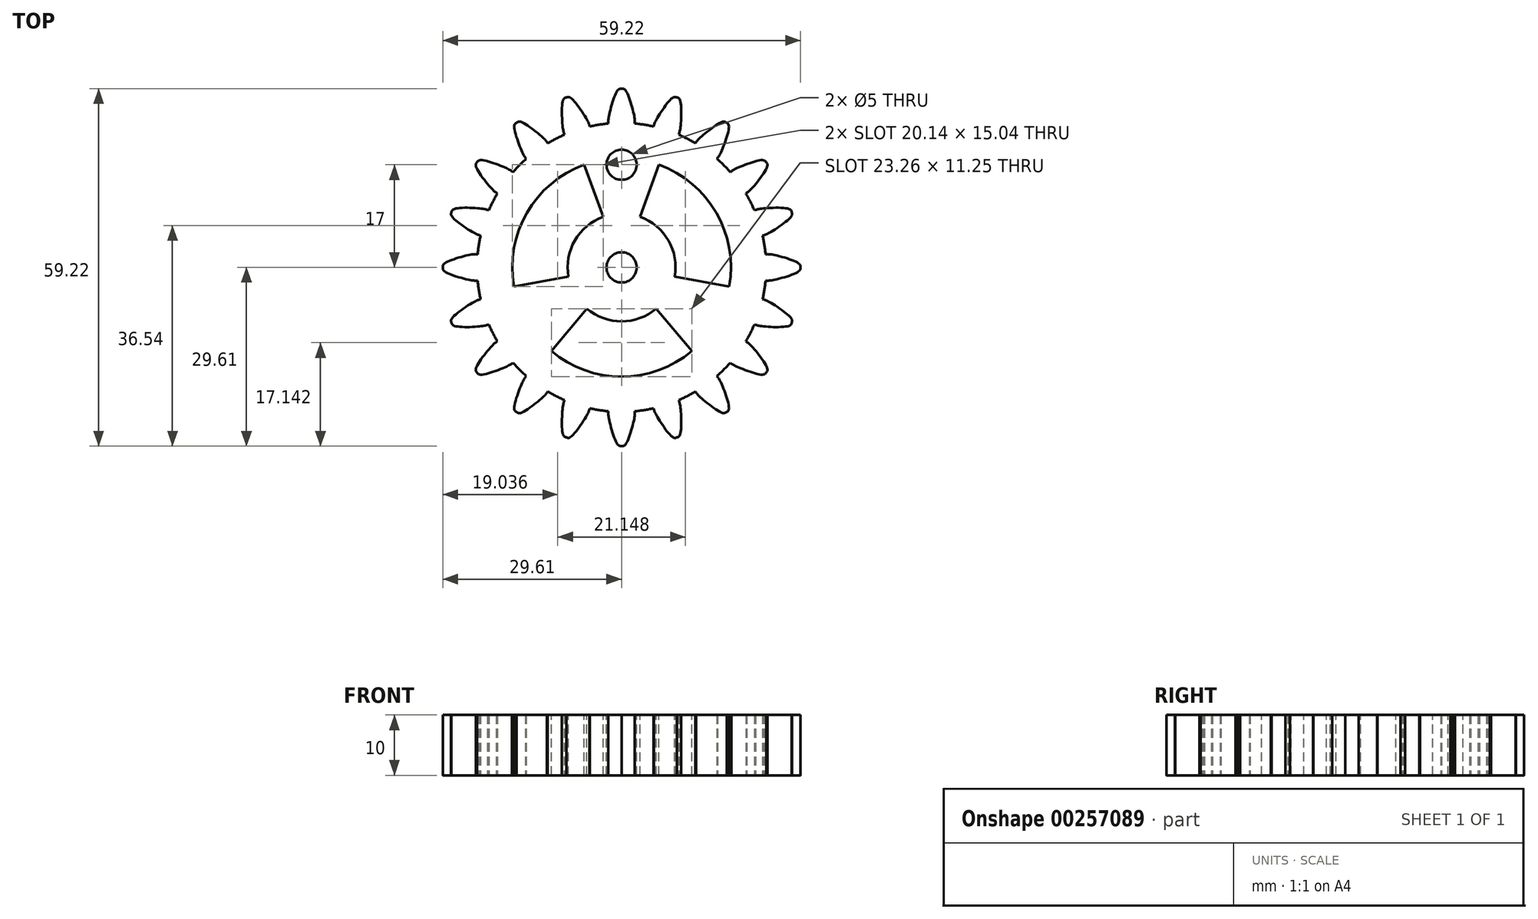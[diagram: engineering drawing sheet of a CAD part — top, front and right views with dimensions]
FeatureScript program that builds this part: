
annotation { "Feature Type Name" : "Feature", "Feature Type Description" : "" }
export const myFeature = defineFeature(function(context is Context, id is Id, definition is map)
    precondition{}
    {
        {
            var Q0;
            Q0=qCreatedBy(makeId("Top.planeOp"),FACE);
            var sketch = newSketch(context, id + "F0", { "sketchPlane" : qUnion([Q0])});
            skLineSegment(sketch, "E0.bottom", {"start": v(-22.39, -2.2) * mm, "end": v(-24.04, -2.2) * mm});
            skLineSegment(sketch, "E0.top", {"start": v(-22.39, 2.2) * mm, "end": v(-24.04, 2.2) * mm});
            skLineSegment(sketch, "E0.left", {"start": v(-22.39, -2.2) * mm, "end": v(-22.39, 2.2) * mm});
            skLineSegment(sketch, "E0.right", {"start": v(-24.04, -2.2) * mm, "end": v(-24.04, 2.2) * mm});
            skPoint(sketch, "E0.middle", {"position": v(-23.21, 0) * mm});
            skFitSpline(sketch, "E1", {"points": [v(-24.04, 2.2) * mm, v(-25.02, 2.1) * mm, v(-29.35, 0.63) * mm, v(-29.6, 0) * mm], "startDerivative": vector(-2.71, 0.04) * mm, "endDerivative": vector(0.07, -2.94) * mm});
            skLineSegment(sketch, "E2", {"start": v(-29.6, 0) * mm, "end": v(-24.04, 0) * mm});
            skFitSpline(sketch, "E3.MirrorCS", {"points": [v(-24.04, -2.2) * mm, v(-25.02, -2.1) * mm, v(-29.35, -0.63) * mm, v(-29.6, 0) * mm], "startDerivative": vector(-2.71, -0.04) * mm, "endDerivative": vector(0.07, 2.94) * mm});
            skCircle(sketch, "E4", {"center": v(0, 0) * mm, "radius": 5.34 * mm});
            skSolve(sketch);
        }
        {
            var Q0;
            Q0=makeQuery(id+"F0.imprint","IMPRINT",FACE,{"disambiguationData":[TD([[makeQuery(id+"F0.imprint","IMPRINT",EDGE,{"derivedFrom":sQuery(id+"F0.wireOp",EDGE,"E4")}),1.0]])]});
            extrude(context, id + "F1", {"entities" : qUnion([Q0]), "depth" : 10 * mm});
        }
        {
            var Q0;
            {var subQ0=sQuery(id+"F0.wireOp",EDGE,"E1");Q0=makeQuery(id+"F0.imprint","IMPRINT",FACE,{"disambiguationData":[TD([[makeQuery(id+"F0.imprint","IMPRINT",EDGE,{"derivedFrom":subQ0}),1.0]])]});}
            var Q1;
            {var subQ1=sQuery(id+"F0.wireOp",EDGE,"E0.bottom");Q1=makeQuery(id+"F0.imprint","IMPRINT",FACE,{"disambiguationData":[TD([[makeQuery(id+"F0.imprint","IMPRINT",EDGE,{"derivedFrom":subQ1}),-1.0]])]});}
            var Q2;
            {var subQ2=sQuery(id+"F0.wireOp",EDGE,"E2");Q2=makeQuery(id+"F0.imprint","IMPRINT",FACE,{"disambiguationData":[TD([[makeQuery(id+"F0.imprint","IMPRINT",EDGE,{"derivedFrom":subQ2}),-1.0]])]});}
            extrude(context, id + "F2", {"entities" : qUnion([Q0, Q1, Q2]), "depth" : 10 * mm});
        }
        {
            var Q0;
            Q0=makeQuery(id+"F2.opExtrude","SWEPT_BODY",BODY,{"disambiguationData":[OSD([sQuery(id+"F0.wireOp",EDGE,"E0.bottom"),sQuery(id+"F0.wireOp",EDGE,"E0.top"),sQuery(id+"F0.wireOp",EDGE,"E0.left"),sQuery(id+"F0.wireOp",EDGE,"E1"),sQuery(id+"F0.wireOp",EDGE,"E3.MirrorCS")])]});
            var Q1;
            Q1=makeQuery(id+"F1.opExtrude","CAP_EDGE",EDGE,{"disambiguationData":[OSD([sQuery(id+"F0.wireOp",EDGE,"E4")])],"isStart":false});
            circularPattern(context, id + "F3", {"entities" : qUnion([Q0]), "axis" : qUnion([Q1]), "angle" : 360 * degree, "instanceCount" : 20, "equalSpace" : true});
        }
        {
            var Q0;
            Q0=qCreatedBy(makeId("Top.planeOp"),FACE);
            var sketch = newSketch(context, id + "F4", { "sketchPlane" : qUnion([Q0])});
            skCircle(sketch, "E5", {"center": v(0, 0) * mm, "radius": 23.92 * mm});
            skSolve(sketch);
        }
        {
            var Q0;
            Q0=makeQuery(id+"F4.imprint","IMPRINT",FACE,{"disambiguationData":[TD([[makeQuery(id+"F4.imprint","IMPRINT",EDGE,{"derivedFrom":sQuery(id+"F4.wireOp",EDGE,"E5")}),1.0]])]});
            extrude(context, id + "F5", {"entities" : qUnion([Q0]), "operationType" : NewBodyOperationType.ADD, "depth" : 10 * mm});
        }
        {
            var Q0;
            {var subQ0=makeQuery(id+"F2.opExtrude","CAP_FACE",FACE,{"disambiguationData":[OSD([sQuery(id+"F0.wireOp",EDGE,"E0.bottom"),sQuery(id+"F0.wireOp",EDGE,"E0.top"),sQuery(id+"F0.wireOp",EDGE,"E0.left"),sQuery(id+"F0.wireOp",EDGE,"E1"),sQuery(id+"F0.wireOp",EDGE,"E3.MirrorCS")])],"isStart":false});Q0=makeQuery(id+"F5.boolean.opBoolean","MERGE",FACE,{"derivedFrom":[makeQuery(id+"F1.opExtrude","CAP_FACE",FACE,{"disambiguationData":[OSD([sQuery(id+"F0.wireOp",EDGE,"E4")])],"isStart":false}),subQ0,makeQuery(id+"F3.opPattern","COPY",FACE,{"derivedFrom":subQ0,"instanceName":"1"}),makeQuery(id+"F3.opPattern","COPY",FACE,{"derivedFrom":subQ0,"instanceName":"2"}),makeQuery(id+"F3.opPattern","COPY",FACE,{"derivedFrom":subQ0,"instanceName":"3"}),makeQuery(id+"F3.opPattern","COPY",FACE,{"derivedFrom":subQ0,"instanceName":"4"}),makeQuery(id+"F3.opPattern","COPY",FACE,{"derivedFrom":subQ0,"instanceName":"5"}),makeQuery(id+"F3.opPattern","COPY",FACE,{"derivedFrom":subQ0,"instanceName":"6"}),makeQuery(id+"F3.opPattern","COPY",FACE,{"derivedFrom":subQ0,"instanceName":"7"}),makeQuery(id+"F3.opPattern","COPY",FACE,{"derivedFrom":subQ0,"instanceName":"8"}),makeQuery(id+"F3.opPattern","COPY",FACE,{"derivedFrom":subQ0,"instanceName":"9"}),makeQuery(id+"F3.opPattern","COPY",FACE,{"derivedFrom":subQ0,"instanceName":"10"}),makeQuery(id+"F3.opPattern","COPY",FACE,{"derivedFrom":subQ0,"instanceName":"11"}),makeQuery(id+"F3.opPattern","COPY",FACE,{"derivedFrom":subQ0,"instanceName":"12"}),makeQuery(id+"F3.opPattern","COPY",FACE,{"derivedFrom":subQ0,"instanceName":"13"}),makeQuery(id+"F3.opPattern","COPY",FACE,{"derivedFrom":subQ0,"instanceName":"14"}),makeQuery(id+"F3.opPattern","COPY",FACE,{"derivedFrom":subQ0,"instanceName":"15"}),makeQuery(id+"F5.opExtrude","CAP_FACE",FACE,{"disambiguationData":[OSD([sQuery(id+"F4.wireOp",EDGE,"E5")])],"isStart":false})]});}
            var sketch = newSketch(context, id + "F6", { "sketchPlane" : qUnion([Q0])});
            skLineSegment(sketch, "E6", {"start": v(0, 0) * mm, "end": v(0, -22.46) * mm, "construction": true});
            skArc(sketch, "E7", {"start": v(-11.63, -13.86) * mm, "mid": v(0, -18.1) * mm, "end": v(11.63, -13.86) * mm});
            skArc(sketch, "E8", {"start": v(-5.74, -6.84) * mm, "mid": v(0, -8.93) * mm, "end": v(5.74, -6.84) * mm});
            skLineSegment(sketch, "E9", {"start": v(-5.74, -6.84) * mm, "end": v(-11.63, -13.86) * mm});
            skLineSegment(sketch, "E10", {"start": v(5.74, -6.84) * mm, "end": v(11.63, -13.86) * mm});
            skArc(sketch, "E11.1.0", {"start": v(8.8, -1.55) * mm, "mid": v(7.74, 4.47) * mm, "end": v(3.06, 8.4) * mm});
            skLineSegment(sketch, "E11.1.1", {"start": v(8.8, -1.55) * mm, "end": v(17.82, -3.14) * mm});
            skArc(sketch, "E11.1.2", {"start": v(17.82, -3.14) * mm, "mid": v(15.67, 9.05) * mm, "end": v(6.19, 17) * mm});
            skLineSegment(sketch, "E11.1.3", {"start": v(3.06, 8.4) * mm, "end": v(6.19, 17) * mm});
            skArc(sketch, "E11.2.0", {"start": v(-3.06, 8.4) * mm, "mid": v(-7.74, 4.47) * mm, "end": v(-8.8, -1.55) * mm});
            skLineSegment(sketch, "E11.2.1", {"start": v(-3.06, 8.4) * mm, "end": v(-6.19, 17) * mm});
            skArc(sketch, "E11.2.2", {"start": v(-6.19, 17) * mm, "mid": v(-15.67, 9.05) * mm, "end": v(-17.82, -3.14) * mm});
            skLineSegment(sketch, "E11.2.3", {"start": v(-8.8, -1.55) * mm, "end": v(-17.82, -3.14) * mm});
            skSolve(sketch);
        }
        {
            var Q0;
            {var subQ0=makeQuery(id+"F2.opExtrude","CAP_FACE",FACE,{"disambiguationData":[OSD([sQuery(id+"F0.wireOp",EDGE,"E0.bottom"),sQuery(id+"F0.wireOp",EDGE,"E0.top"),sQuery(id+"F0.wireOp",EDGE,"E0.left"),sQuery(id+"F0.wireOp",EDGE,"E1"),sQuery(id+"F0.wireOp",EDGE,"E3.MirrorCS")])],"isStart":false});Q0=makeQuery(id+"F5.boolean.opBoolean","MERGE",FACE,{"derivedFrom":[makeQuery(id+"F1.opExtrude","CAP_FACE",FACE,{"disambiguationData":[OSD([sQuery(id+"F0.wireOp",EDGE,"E4")])],"isStart":false}),subQ0,makeQuery(id+"F3.opPattern","COPY",FACE,{"derivedFrom":subQ0,"instanceName":"1"}),makeQuery(id+"F3.opPattern","COPY",FACE,{"derivedFrom":subQ0,"instanceName":"2"}),makeQuery(id+"F3.opPattern","COPY",FACE,{"derivedFrom":subQ0,"instanceName":"3"}),makeQuery(id+"F3.opPattern","COPY",FACE,{"derivedFrom":subQ0,"instanceName":"4"}),makeQuery(id+"F3.opPattern","COPY",FACE,{"derivedFrom":subQ0,"instanceName":"5"}),makeQuery(id+"F3.opPattern","COPY",FACE,{"derivedFrom":subQ0,"instanceName":"6"}),makeQuery(id+"F3.opPattern","COPY",FACE,{"derivedFrom":subQ0,"instanceName":"7"}),makeQuery(id+"F3.opPattern","COPY",FACE,{"derivedFrom":subQ0,"instanceName":"8"}),makeQuery(id+"F3.opPattern","COPY",FACE,{"derivedFrom":subQ0,"instanceName":"9"}),makeQuery(id+"F3.opPattern","COPY",FACE,{"derivedFrom":subQ0,"instanceName":"10"}),makeQuery(id+"F3.opPattern","COPY",FACE,{"derivedFrom":subQ0,"instanceName":"11"}),makeQuery(id+"F3.opPattern","COPY",FACE,{"derivedFrom":subQ0,"instanceName":"12"}),makeQuery(id+"F3.opPattern","COPY",FACE,{"derivedFrom":subQ0,"instanceName":"13"}),makeQuery(id+"F3.opPattern","COPY",FACE,{"derivedFrom":subQ0,"instanceName":"14"}),makeQuery(id+"F3.opPattern","COPY",FACE,{"derivedFrom":subQ0,"instanceName":"15"}),makeQuery(id+"F5.opExtrude","CAP_FACE",FACE,{"disambiguationData":[OSD([sQuery(id+"F4.wireOp",EDGE,"E5")])],"isStart":false})]});}
            var sketch = newSketch(context, id + "F7", { "sketchPlane" : qUnion([Q0])});
            skCircle(sketch, "E12", {"center": v(0, 0) * mm, "radius": 2.5 * mm});
            skCircle(sketch, "E13.1.0.0", {"center": v(0, 17) * mm, "radius": 2.5 * mm});
            skLineSegment(sketch, "E13.direction1", {"start": v(0, 0) * mm, "end": v(0, 17) * mm, "construction": true});
            skSolve(sketch);
        }
        {
            var Q0;
            Q0=makeQuery(id+"F6.imprint","IMPRINT",FACE,{"disambiguationData":[TD([[makeQuery(id+"F6.imprint","IMPRINT",EDGE,{"derivedFrom":sQuery(id+"F6.wireOp",EDGE,"E11.2.0")}),-1.0]])]});
            var Q1;
            Q1=makeQuery(id+"F6.imprint","IMPRINT",FACE,{"disambiguationData":[TD([[makeQuery(id+"F6.imprint","IMPRINT",EDGE,{"derivedFrom":sQuery(id+"F6.wireOp",EDGE,"E7")}),1.0]])]});
            var Q2;
            Q2=makeQuery(id+"F6.imprint","IMPRINT",FACE,{"disambiguationData":[TD([[makeQuery(id+"F6.imprint","IMPRINT",EDGE,{"derivedFrom":sQuery(id+"F6.wireOp",EDGE,"E11.1.0")}),-1.0]])]});
            extrude(context, id + "F8", {"entities" : qUnion([Q0, Q1, Q2]), "operationType" : NewBodyOperationType.REMOVE, "endBound" : BoundingType.UP_TO_NEXT, "oppositeDirection" : true, "depth" : 25 * mm});
        }
        {
            var Q0;
            Q0=makeQuery(id+"F7.imprint","IMPRINT",FACE,{"disambiguationData":[TD([[makeQuery(id+"F7.imprint","IMPRINT",EDGE,{"derivedFrom":sQuery(id+"F7.wireOp",EDGE,"E13.1.0.0")}),1.0]])]});
            var Q1;
            Q1=makeQuery(id+"F7.imprint","IMPRINT",FACE,{"disambiguationData":[TD([[makeQuery(id+"F7.imprint","IMPRINT",EDGE,{"derivedFrom":sQuery(id+"F7.wireOp",EDGE,"E12")}),1.0]])]});
            extrude(context, id + "F9", {"entities" : qUnion([Q0, Q1]), "operationType" : NewBodyOperationType.REMOVE, "endBound" : BoundingType.UP_TO_NEXT, "oppositeDirection" : true, "depth" : 25 * mm});
        }
    });
